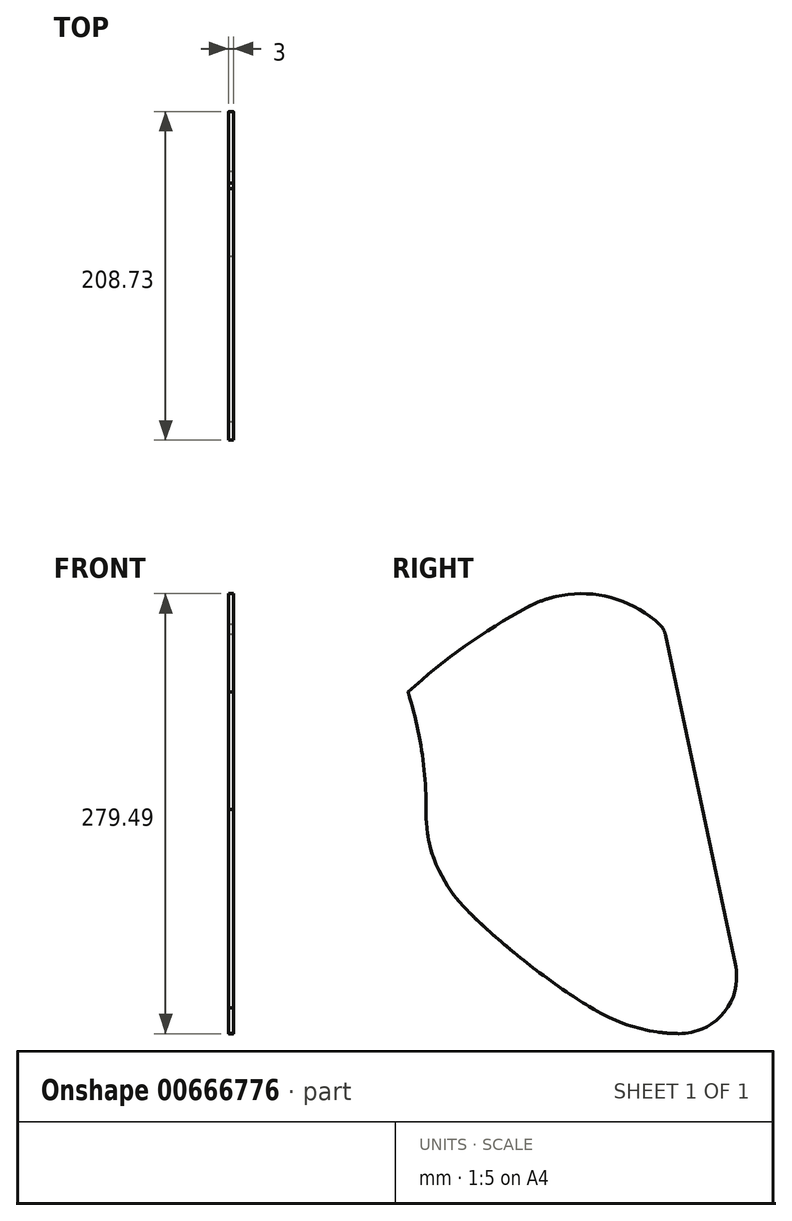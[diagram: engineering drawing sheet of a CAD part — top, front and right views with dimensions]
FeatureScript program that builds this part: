
annotation { "Feature Type Name" : "Feature", "Feature Type Description" : "" }
export const myFeature = defineFeature(function(context is Context, id is Id, definition is map)
    precondition{}
    {
        {
            var Q0;
            Q0=qCreatedBy(makeId("Right.planeOp"),FACE);
            var sketch = newSketch(context, id + "F0", { "sketchPlane" : qUnion([Q0])});
            skFitSpline(sketch, "E0.0.0", {"points": [v(85.03, -159.67) * mm, v(86.53, -159.72) * mm, v(88.77, -159.67) * mm, v(91.36, -159.4) * mm, v(92.84, -159.17) * mm, v(94.31, -158.9) * mm, v(96.13, -158.5) * mm, v(99.01, -157.69) * mm, v(102.5, -156.37) * mm, v(106.5, -154.32) * mm, v(111.5, -151.02) * mm, v(116.97, -145.87) * mm, v(122, -138.38) * mm, v(124.68, -131.36) * mm, v(125.84, -125.5) * mm, v(126.22, -121.02) * mm, v(126.1, -116.54) * mm, v(125.67, -113.58) * mm, v(125.37, -112.11) * mm]});
            skFitSpline(sketch, "E0.0.1", {"points": [v(125.43, -112.38) * mm, v(107.3, -27.05) * mm, v(89.16, 58.28) * mm, v(71.03, 143.61) * mm]});
            skFitSpline(sketch, "E0.0.2", {"points": [v(71.07, 143.42) * mm, v(70.97, 143.92) * mm, v(70.75, 144.66) * mm, v(70.35, 145.6) * mm, v(70, 146.28) * mm, v(69.6, 146.94) * mm, v(69, 147.76) * mm, v(68.48, 148.32) * mm, v(68.1, 148.67) * mm]});
            skFitSpline(sketch, "E0.0.3", {"points": [v(68.1, 148.67) * mm, v(66.5, 150.16) * mm, v(64.04, 152.28) * mm, v(60.59, 154.91) * mm, v(57.92, 156.79) * mm, v(55.18, 158.56) * mm, v(52.38, 160.22) * mm, v(49.52, 161.77) * mm, v(46.6, 163.2) * mm, v(43.61, 164.53) * mm, v(40.59, 165.74) * mm, v(37.52, 166.83) * mm, v(34.4, 167.8) * mm, v(31.26, 168.64) * mm, v(28.08, 169.36) * mm, v(24.89, 169.96) * mm, v(21.66, 170.44) * mm, v(18.42, 170.78) * mm, v(15.17, 171) * mm, v(11.92, 171.1) * mm, v(8.65, 171.07) * mm, v(5.4, 170.91) * mm, v(2.15, 170.63) * mm, v(-1.07, 170.22) * mm, v(-4.3, 169.68) * mm, v(-7.48, 169.02) * mm, v(-10.64, 168.23) * mm, v(-13.77, 167.33) * mm, v(-16.86, 166.3) * mm, v(-19.92, 165.15) * mm, v(-23.92, 163.47) * mm, v(-26.84, 162.03) * mm, v(-28.75, 161) * mm]});
            skFitSpline(sketch, "E0.0.8", {"points": [v(-104.3, 9.13) * mm, v(-104.32, 7.36) * mm, v(-104.26, 3.82) * mm, v(-103.9, -1.48) * mm, v(-103.27, -6.75) * mm, v(-102.38, -11.98) * mm, v(-101.22, -17.17) * mm, v(-99.8, -22.28) * mm, v(-98.13, -27.32) * mm, v(-96.2, -32.27) * mm, v(-94.04, -37.12) * mm, v(-91.62, -41.85) * mm, v(-88.98, -46.45) * mm, v(-86.1, -50.92) * mm, v(-83, -55.23) * mm, v(-79.69, -59.38) * mm, v(-76.17, -63.36) * mm, v(-73.7, -65.9) * mm, v(-72.43, -67.13) * mm]});
            skFitSpline(sketch, "E0.0.9", {"points": [v(-72.44, -67.12) * mm, v(-65.3, -74.06) * mm, v(-54.3, -84.18) * mm, v(-41.03, -95.45) * mm, v(-33.31, -101.74) * mm, v(-27.46, -106.39) * mm, v(-21.54, -110.95) * mm, v(-13.57, -116.92) * mm, v(0.58, -127.08) * mm, v(13.05, -135.3) * mm, v(21.51, -140.56) * mm]});
            skFitSpline(sketch, "E0.0.10", {"points": [v(21.51, -140.56) * mm, v(23.9, -142.03) * mm, v(27.53, -144.13) * mm, v(32.5, -146.67) * mm, v(36.3, -148.46) * mm, v(40.15, -150.13) * mm, v(44.05, -151.66) * mm, v(48, -153.06) * mm, v(52, -154.34) * mm, v(56.04, -155.48) * mm, v(60.1, -156.5) * mm, v(64.2, -157.36) * mm, v(68.34, -158.1) * mm, v(72.5, -158.7) * mm, v(78.05, -159.33) * mm, v(82.24, -159.59) * mm, v(85.04, -159.67) * mm]});
            skArc(sketch, "E1", {"start": v(-28.75, 161) * mm, "mid": v(-75, 132.3) * mm, "end": v(-117.51, 98.34) * mm});
            skArc(sketch, "E2", {"start": v(-104.3, 9.13) * mm, "mid": v(-107.6, 54.22) * mm, "end": v(-117.51, 98.34) * mm});
            skFitSpline(sketch, "E3.0", {"points": [v(71.5, 152.34) * mm, v(69.82, 153.9) * mm, v(67.2, 156.16) * mm, v(63.54, 158.95) * mm, v(60.72, 160.93) * mm, v(57.81, 162.81) * mm, v(54.85, 164.57) * mm, v(51.81, 166.21) * mm, v(48.71, 167.74) * mm, v(45.55, 169.14) * mm, v(42.35, 170.42) * mm, v(39.1, 171.57) * mm, v(35.8, 172.6) * mm, v(32.46, 173.5) * mm, v(29.1, 174.26) * mm, v(25.7, 174.9) * mm, v(22.29, 175.4) * mm, v(18.85, 175.77) * mm, v(15.41, 176) * mm, v(11.96, 176.1) * mm, v(8.5, 176.07) * mm, v(5.06, 175.9) * mm, v(1.62, 175.6) * mm, v(-1.8, 175.16) * mm, v(-5.21, 174.6) * mm, v(-8.6, 173.9) * mm, v(-11.94, 173.06) * mm, v(-15.25, 172.1) * mm, v(-18.53, 171.01) * mm, v(-21.77, 169.8) * mm, v(-26, 168.01) * mm, v(-29.1, 166.49) * mm, v(-31.13, 165.39) * mm]});
            skFitSpline(sketch, "E3.1", {"points": [v(75.96, 144.45) * mm, v(75.8, 145.2) * mm, v(75.38, 146.68) * mm, v(74.4, 148.77) * mm, v(73.1, 150.68) * mm, v(72.07, 151.81) * mm, v(71.5, 152.34) * mm]});
            skArc(sketch, "E3.2", {"start": v(-31.13, 165.39) * mm, "mid": v(-79.18, 135.46) * mm, "end": v(-123.23, 99.9) * mm});
            skFitSpline(sketch, "E3.3", {"points": [v(130.32, -111.34) * mm, v(112.19, -26.01) * mm, v(94.06, 59.32) * mm, v(75.92, 144.65) * mm]});
            skFitSpline(sketch, "E3.4", {"points": [v(84.86, -164.66) * mm, v(86.54, -164.72) * mm, v(89.06, -164.67) * mm, v(92.4, -164.3) * mm, v(94.9, -163.9) * mm, v(97.36, -163.35) * mm, v(100.6, -162.43) * mm, v(106.11, -160.36) * mm, v(113.42, -156.09) * mm, v(120.81, -149.13) * mm, v(126.47, -140.7) * mm, v(130.1, -131.22) * mm, v(131.28, -122.84) * mm, v(131.08, -116.11) * mm, v(130.6, -112.78) * mm, v(130.28, -111.13) * mm]});
            skArc(sketch, "E3.5", {"start": v(-109.3, 9.15) * mm, "mid": v(-112.78, 55.06) * mm, "end": v(-123.23, 99.9) * mm});
            skFitSpline(sketch, "E3.6", {"points": [v(-109.3, 9.17) * mm, v(-109.32, 7.32) * mm, v(-109.26, 3.6) * mm, v(-108.75, -3.8) * mm, v(-106.9, -16.65) * mm, v(-102.56, -30.9) * mm, v(-96.14, -44.3) * mm, v(-90.35, -53.81) * mm, v(-84.75, -61.21) * mm, v(-79.84, -66.77) * mm, v(-77.24, -69.42) * mm, v(-75.91, -70.71) * mm]});
            skFitSpline(sketch, "E3.7", {"points": [v(-75.92, -70.7) * mm, v(-68.71, -77.71) * mm, v(-57.63, -87.92) * mm, v(-42.32, -100.92) * mm, v(-30.57, -110.36) * mm, v(-18.56, -119.5) * mm, v(-2.25, -131.2) * mm, v(10.33, -139.5) * mm, v(18.88, -144.8) * mm]});
            skFitSpline(sketch, "E3.8", {"points": [v(18.88, -144.8) * mm, v(21.35, -146.34) * mm, v(25.12, -148.51) * mm, v(30.3, -151.16) * mm, v(34.24, -153.02) * mm, v(38.25, -154.75) * mm, v(42.3, -156.34) * mm, v(46.4, -157.8) * mm, v(50.56, -159.13) * mm, v(54.76, -160.32) * mm, v(58.99, -161.36) * mm, v(63.25, -162.27) * mm, v(67.54, -163.04) * mm, v(71.86, -163.67) * mm, v(77.63, -164.31) * mm, v(81.98, -164.58) * mm, v(84.9, -164.66) * mm]});
            skSolve(sketch);
        }
        {
            var Q0;
            Q0=qSketchRegion(id+"F0",true);
            extrude(context, id + "F1", {"entities" : qUnion([Q0]), "depth" : 192.68 * mm, "offsetDistance" : 25 * mm});
        }
        {
            var Q0;
            Q0=makeQuery(id+"F1.opExtrude","SWEPT_BODY",BODY,{"disambiguationData":[OSD([sQuery(id+"F0.wireOp",EDGE,"E0.0.0"),sQuery(id+"F0.wireOp",EDGE,"E0.0.1"),sQuery(id+"F0.wireOp",EDGE,"E0.0.2"),sQuery(id+"F0.wireOp",EDGE,"E0.0.3"),sQuery(id+"F0.wireOp",EDGE,"E0.0.8"),sQuery(id+"F0.wireOp",EDGE,"E0.0.9"),sQuery(id+"F0.wireOp",EDGE,"E0.0.10"),sQuery(id+"F0.wireOp",EDGE,"E1"),sQuery(id+"F0.wireOp",EDGE,"E2")])]});
            var Q1;
            Q1=qCreatedBy(makeId("Origin.pointOp"),VERTEX);
            var Q2;
            Q2=qCreatedBy(makeId("Origin.pointOp"),VERTEX);
            transform(context, id + "F2", {"entities" : qUnion([Q0]), "transformType" : TransformType.SCALE_UNIFORMLY, "scale" : 0.82, "scalePoint" : qUnion([Q2]), "makeCopy" : false});
        }
        {
            var Q0;
            Q0=makeQuery(id+"F1.opExtrude","SWEPT_FACE",FACE,{"disambiguationData":[OSD([sQuery(id+"F0.wireOp",EDGE,"E3.3")])]});
            var sketch = newSketch(context, id + "F3", { "sketchPlane" : qUnion([Q0])});
            skFitSpline(sketch, "E4.0", {"points": [v(-158, -111.52) * mm, v(-158, -39.99) * mm, v(-158, 31.55) * mm, v(-158, 103.08) * mm], "construction": true});
            skFitSpline(sketch, "E5.0", {"points": [v(0, -111.52) * mm, v(0, -39.99) * mm, v(0, 31.55) * mm, v(0, 103.08) * mm], "construction": true});
            skCircle(sketch, "E6", {"center": v(-79, -26.35) * mm, "radius": 32.5 * mm});
            skSolve(sketch);
        }
        {
            var Q0;
            Q0=makeQuery(id+"F1.opExtrude","SWEPT_FACE",FACE,{"disambiguationData":[OSD([sQuery(id+"F0.wireOp",EDGE,"E3.3")])]});
            var sketch = newSketch(context, id + "F4", { "sketchPlane" : qUnion([Q0])});
            skCircle(sketch, "E7", {"center": v(-82, -21.35) * mm, "radius": 30 * mm});
            skFitSpline(sketch, "E8.0", {"points": [v(-158, -111.52) * mm, v(-158, -39.99) * mm, v(-158, 31.55) * mm, v(-158, 103.08) * mm], "construction": true});
            skFitSpline(sketch, "E9.0", {"points": [v(0, -111.52) * mm, v(0, -39.99) * mm, v(0, 31.55) * mm, v(0, 103.08) * mm], "construction": true});
            skSolve(sketch);
        }
        {
            var Q0;
            Q0=qSketchRegion(id+"F3",true);
            extrude(context, id + "F5", {"entities" : qUnion([Q0]), "operationType" : NewBodyOperationType.REMOVE, "oppositeDirection" : true, "depth" : 25 * mm, "offsetDistance" : 25 * mm});
        }
        {
            var Q0;
            Q0=qCreatedBy(makeId("Right.planeOp"),FACE);
            cPlane(context, id + "F6", {"entities" : qUnion([Q0]), "cplaneType" : CPlaneType.OFFSET, "offset" : 3 * mm, "width" : 150 * mm, "height" : 150 * mm});
        }
        {
            var Q0;
            Q0=qCreatedBy(makeId("Right.planeOp"),FACE);
            var sketch = newSketch(context, id + "F7", { "sketchPlane" : qUnion([Q0])});
            skFitSpline(sketch, "E10.0.0", {"points": [v(-62.26, -57.98) * mm, v(-56.34, -63.72) * mm, v(-47.26, -72.1) * mm, v(-34.7, -82.75) * mm, v(-25.06, -90.5) * mm, v(-15.22, -97.98) * mm, v(-1.85, -107.6) * mm, v(8.47, -114.39) * mm, v(15.48, -118.74) * mm]});
            skFitSpline(sketch, "E10.0.1", {"points": [v(15.48, -118.74) * mm, v(17.5, -120) * mm, v(20.6, -121.78) * mm, v(24.84, -123.95) * mm, v(28.08, -125.48) * mm, v(31.36, -126.9) * mm, v(34.69, -128.2) * mm, v(38.05, -129.4) * mm, v(41.46, -130.49) * mm, v(44.9, -131.46) * mm, v(48.37, -132.32) * mm, v(51.86, -133.06) * mm, v(55.38, -133.7) * mm, v(58.92, -134.2) * mm, v(63.66, -134.74) * mm, v(67.23, -134.96) * mm, v(69.61, -135.02) * mm]});
            skFitSpline(sketch, "E10.0.2", {"points": [v(69.58, -135.02) * mm, v(70.96, -135.07) * mm, v(73.03, -135.03) * mm, v(75.77, -134.73) * mm, v(77.82, -134.4) * mm, v(79.83, -133.95) * mm, v(82.49, -133.2) * mm, v(87.01, -131.5) * mm, v(93, -128) * mm, v(99.07, -122.29) * mm, v(103.7, -115.38) * mm, v(106.68, -107.6) * mm, v(107.65, -100.73) * mm, v(107.49, -95.21) * mm, v(107.1, -92.48) * mm, v(106.83, -91.12) * mm]});
            skFitSpline(sketch, "E10.0.3", {"points": [v(106.86, -91.3) * mm, v(92, -21.33) * mm, v(77.13, 48.64) * mm, v(62.26, 118.61) * mm], "construction": true});
            skFitSpline(sketch, "E10.0.4", {"points": [v(62.3, 118.45) * mm, v(62.16, 119.06) * mm, v(61.8, 120.27) * mm, v(61, 121.99) * mm, v(59.95, 123.56) * mm, v(59.1, 124.49) * mm, v(58.63, 124.92) * mm]});
            skFitSpline(sketch, "E10.0.5", {"points": [v(58.63, 124.92) * mm, v(57.25, 126.2) * mm, v(55.1, 128.05) * mm, v(52.1, 130.34) * mm, v(49.79, 131.97) * mm, v(47.4, 133.5) * mm, v(44.97, 134.95) * mm, v(42.49, 136.3) * mm, v(39.94, 137.54) * mm, v(37.36, 138.7) * mm, v(34.73, 139.74) * mm, v(32.06, 140.69) * mm, v(29.36, 141.53) * mm, v(26.62, 142.27) * mm, v(23.86, 142.9) * mm, v(21.08, 143.41) * mm, v(18.28, 143.83) * mm, v(15.46, 144.13) * mm, v(12.64, 144.32) * mm, v(9.81, 144.4) * mm, v(6.98, 144.38) * mm, v(4.15, 144.24) * mm, v(1.33, 144) * mm, v(-1.48, 143.64) * mm, v(-4.27, 143.17) * mm, v(-7.05, 142.6) * mm, v(-9.8, 141.91) * mm, v(-12.5, 141.13) * mm, v(-15.2, 140.23) * mm, v(-17.85, 139.23) * mm, v(-21.33, 137.77) * mm, v(-23.87, 136.52) * mm, v(-25.53, 135.62) * mm]});
            skArc(sketch, "E10.0.6", {"start": v(-25.53, 135.62) * mm, "mid": v(-64.93, 111.07) * mm, "end": v(-101.05, 81.92) * mm, "construction": true});
            skArc(sketch, "E10.0.7", {"start": v(-101.05, 81.92) * mm, "mid": v(-92.48, 45.15) * mm, "end": v(-89.63, 7.5) * mm, "construction": true});
            skFitSpline(sketch, "E10.0.8", {"points": [v(-89.63, 7.52) * mm, v(-89.64, 6) * mm, v(-89.6, 2.96) * mm, v(-89.18, -3.1) * mm, v(-87.65, -13.65) * mm, v(-84.1, -25.35) * mm, v(-78.84, -36.33) * mm, v(-74.09, -44.13) * mm, v(-69.5, -50.2) * mm, v(-65.46, -54.75) * mm, v(-63.34, -56.92) * mm, v(-62.25, -57.98) * mm], "construction": true});
            skArc(sketch, "E11.0", {"start": v(-96.36, 80.64) * mm, "mid": v(-88.17, 44.08) * mm, "end": v(-85.54, 6.7) * mm});
            skArc(sketch, "E11.1", {"start": v(-23.58, 132.01) * mm, "mid": v(-61.5, 108.48) * mm, "end": v(-96.36, 80.64) * mm});
            skFitSpline(sketch, "E11.2", {"points": [v(-85.53, 7.49) * mm, v(-85.54, 6.04) * mm, v(-85.5, 3.14) * mm, v(-85.1, -2.66) * mm, v(-83.64, -12.72) * mm, v(-80.25, -23.89) * mm, v(-75.23, -34.37) * mm, v(-70.7, -41.81) * mm, v(-66.3, -47.6) * mm, v(-62.46, -51.96) * mm, v(-60.43, -54.03) * mm, v(-59.4, -55.04) * mm]});
            skFitSpline(sketch, "E11.3", {"points": [v(55.84, 121.91) * mm, v(54.53, 123.13) * mm, v(52.5, 124.87) * mm, v(49.68, 127.03) * mm, v(47.5, 128.57) * mm, v(45.25, 130.02) * mm, v(42.95, 131.38) * mm, v(40.6, 132.65) * mm, v(38.2, 133.83) * mm, v(35.76, 134.92) * mm, v(33.28, 135.9) * mm, v(30.77, 136.8) * mm, v(28.21, 137.6) * mm, v(25.63, 138.29) * mm, v(23.03, 138.88) * mm, v(20.4, 139.37) * mm, v(17.76, 139.76) * mm, v(15.1, 140.04) * mm, v(12.44, 140.23) * mm, v(9.77, 140.3) * mm, v(7.1, 140.28) * mm, v(4.43, 140.15) * mm, v(1.77, 139.91) * mm, v(-0.88, 139.58) * mm, v(-3.52, 139.14) * mm, v(-6.14, 138.6) * mm, v(-8.73, 137.95) * mm, v(-11.3, 137.2) * mm, v(-13.83, 136.37) * mm, v(-16.33, 135.42) * mm, v(-19.61, 134.04) * mm, v(-22, 132.86) * mm, v(-23.58, 132.01) * mm]});
            skFitSpline(sketch, "E11.4", {"points": [v(58.28, 117.6) * mm, v(58.2, 118.01) * mm, v(58.02, 118.62) * mm, v(57.7, 119.39) * mm, v(57.4, 119.95) * mm, v(57.07, 120.49) * mm, v(56.58, 121.16) * mm, v(56.15, 121.63) * mm, v(55.84, 121.91) * mm]});
            skFitSpline(sketch, "E11.5", {"points": [v(-59.4, -55.04) * mm, v(-53.54, -60.73) * mm, v(-44.53, -69.03) * mm, v(-32.1, -79.6) * mm, v(-22.54, -87.27) * mm, v(-12.78, -94.68) * mm, v(0.47, -104.2) * mm, v(10.7, -110.95) * mm, v(17.64, -115.26) * mm]});
            skFitSpline(sketch, "E11.6", {"points": [v(17.64, -115.26) * mm, v(19.6, -116.47) * mm, v(22.57, -118.18) * mm, v(26.65, -120.27) * mm, v(29.76, -121.74) * mm, v(32.92, -123.1) * mm, v(36.12, -124.36) * mm, v(39.36, -125.51) * mm, v(42.64, -126.56) * mm, v(45.95, -127.5) * mm, v(49.29, -128.32) * mm, v(52.65, -129.04) * mm, v(56.04, -129.64) * mm, v(59.45, -130.14) * mm, v(64, -130.65) * mm, v(67.43, -130.86) * mm, v(69.73, -130.93) * mm]});
            skFitSpline(sketch, "E11.7", {"points": [v(69.72, -130.93) * mm, v(70.95, -130.97) * mm, v(72.79, -130.93) * mm, v(75.22, -130.67) * mm, v(77.04, -130.37) * mm, v(78.83, -129.97) * mm, v(81.19, -129.3) * mm, v(85.2, -127.8) * mm, v(90.53, -124.68) * mm, v(95.91, -119.61) * mm, v(100.03, -113.47) * mm, v(102.68, -106.57) * mm, v(103.54, -100.46) * mm, v(103.4, -95.56) * mm, v(103.05, -93.13) * mm, v(102.8, -91.93) * mm]});
            skFitSpline(sketch, "E11.8", {"points": [v(102.85, -92.15) * mm, v(87.98, -22.18) * mm, v(73.12, 47.79) * mm, v(58.25, 117.76) * mm]});
            skSolve(sketch);
        }
        {
            var Q0;
            Q0=qCreatedBy(id+"F6.planeOp",FACE);
            var sketch = newSketch(context, id + "F8", { "sketchPlane" : qUnion([Q0])});
            skLineSegment(sketch, "E12", {"start": v(-96.16, 80.21) * mm, "end": v(-25.08, -79.7) * mm});
            skLineSegment(sketch, "E13", {"start": v(-25.08, -79.7) * mm, "end": v(-58.13, -94.4) * mm});
            skLineSegment(sketch, "E14", {"start": v(-58.13, -94.4) * mm, "end": v(-129.2, 65.52) * mm});
            skLineSegment(sketch, "E15", {"start": v(-129.2, 65.52) * mm, "end": v(-96.16, 80.21) * mm});
            skSolve(sketch);
        }
        {
            var Q0;
            Q0=qSketchRegion(id+"F8",true);
            extrude(context, id + "F9", {"entities" : qUnion([Q0]), "operationType" : NewBodyOperationType.REMOVE, "depth" : 158 * mm, "offsetDistance" : 25 * mm, "hasSecondDirection" : true, "secondDirectionOppositeDirection" : true, "secondDirectionDepth" : 25 * mm});
        }
        {
            var Q0;
            Q0=makeQuery(id+"F1.opExtrude","CAP_FACE",FACE,{"disambiguationData":[OSD([sQuery(id+"F0.wireOp",EDGE,"E0.0.0"),sQuery(id+"F0.wireOp",EDGE,"E0.0.1"),sQuery(id+"F0.wireOp",EDGE,"E0.0.2"),sQuery(id+"F0.wireOp",EDGE,"E0.0.3"),sQuery(id+"F0.wireOp",EDGE,"E0.0.8"),sQuery(id+"F0.wireOp",EDGE,"E0.0.9"),sQuery(id+"F0.wireOp",EDGE,"E0.0.10"),sQuery(id+"F0.wireOp",EDGE,"E1"),sQuery(id+"F0.wireOp",EDGE,"E2"),sQuery(id+"F0.wireOp",EDGE,"E3.0"),sQuery(id+"F0.wireOp",EDGE,"E3.1"),sQuery(id+"F0.wireOp",EDGE,"E3.2"),sQuery(id+"F0.wireOp",EDGE,"E3.3"),sQuery(id+"F0.wireOp",EDGE,"E3.4"),sQuery(id+"F0.wireOp",EDGE,"E3.5"),sQuery(id+"F0.wireOp",EDGE,"E3.6"),sQuery(id+"F0.wireOp",EDGE,"E3.7"),sQuery(id+"F0.wireOp",EDGE,"E3.8")])],"isStart":false});
            var sketch = newSketch(context, id + "F10", { "sketchPlane" : qUnion([Q0])});
            skLineSegment(sketch, "E16", {"start": v(-96.22, 80.18) * mm, "end": v(-29.48, -81.66) * mm, "construction": true});
            skLineSegment(sketch, "E17.0", {"start": v(-89.75, 82.85) * mm, "end": v(-23.01, -79) * mm, "construction": true});
            skLineSegment(sketch, "E18", {"start": v(-96.22, 80.18) * mm, "end": v(-96.89, 81.67) * mm});
            skLineSegment(sketch, "E19", {"start": v(-96.89, 81.67) * mm, "end": v(-91.34, 86.7) * mm});
            skLineSegment(sketch, "E20", {"start": v(-89.75, 82.85) * mm, "end": v(-91.34, 86.7) * mm});
            skLineSegment(sketch, "E21", {"start": v(-89.75, 82.85) * mm, "end": v(-17.3, -92.82) * mm});
            skLineSegment(sketch, "E22", {"start": v(-17.3, -92.82) * mm, "end": v(-29.48, -83.53) * mm});
            skLineSegment(sketch, "E23", {"start": v(-29.48, -83.53) * mm, "end": v(-29.48, -81.66) * mm});
            skLineSegment(sketch, "E24", {"start": v(-29.48, -81.66) * mm, "end": v(-96.22, 80.18) * mm});
            skLineSegment(sketch, "E25", {"start": v(-94.61, 76.28) * mm, "end": v(-88.21, 79.12) * mm});
            skLineSegment(sketch, "E26", {"start": v(-30.73, -78.64) * mm, "end": v(-24.26, -75.97) * mm});
            skSolve(sketch);
        }
        {
            var Q0;
            {var subQ0=sQuery(id+"F10.wireOp",EDGE,"E25");Q0=makeQuery(id+"F10.imprint","IMPRINT",FACE,{"disambiguationData":[TD([[makeQuery(id+"F10.imprint","IMPRINT",EDGE,{"derivedFrom":subQ0}),1.0]])]});}
            var Q1;
            {var subQ0=sQuery(id+"F10.wireOp",EDGE,"E26");Q1=makeQuery(id+"F10.imprint","IMPRINT",FACE,{"disambiguationData":[TD([[makeQuery(id+"F10.imprint","IMPRINT",EDGE,{"derivedFrom":subQ0}),-1.0]])]});}
            extrude(context, id + "F11", {"entities" : qUnion([Q0, Q1]), "operationType" : NewBodyOperationType.ADD, "oppositeDirection" : true, "depth" : 158 * mm, "offsetDistance" : 25 * mm});
        }
        {
            var Q0;
            {var subQ0=sQuery(id+"F10.wireOp",EDGE,"E24");var subQ1=sQuery(id+"F10.wireOp",EDGE,"E21");var subQ2=sQuery(id+"F0.wireOp",EDGE,"E0.0.9");var subQ3=sQuery(id+"F0.wireOp",EDGE,"E2");var subQ4=sQuery(id+"F0.wireOp",EDGE,"E1");Q0=makeQuery(id+"F11.boolean.opBoolean","MERGE",FACE,{"derivedFrom":[makeQuery(id+"F1.opExtrude","CAP_FACE",FACE,{"disambiguationData":[OSD([sQuery(id+"F0.wireOp",EDGE,"E0.0.0"),sQuery(id+"F0.wireOp",EDGE,"E0.0.1"),sQuery(id+"F0.wireOp",EDGE,"E0.0.2"),sQuery(id+"F0.wireOp",EDGE,"E0.0.3"),sQuery(id+"F0.wireOp",EDGE,"E0.0.8"),subQ2,sQuery(id+"F0.wireOp",EDGE,"E0.0.10"),subQ4,subQ3,sQuery(id+"F0.wireOp",EDGE,"E3.0"),sQuery(id+"F0.wireOp",EDGE,"E3.1"),sQuery(id+"F0.wireOp",EDGE,"E3.2"),sQuery(id+"F0.wireOp",EDGE,"E3.3"),sQuery(id+"F0.wireOp",EDGE,"E3.4"),sQuery(id+"F0.wireOp",EDGE,"E3.5"),sQuery(id+"F0.wireOp",EDGE,"E3.6"),sQuery(id+"F0.wireOp",EDGE,"E3.7"),sQuery(id+"F0.wireOp",EDGE,"E3.8")])],"isStart":false}),makeQuery(id+"F11.opExtrude","CAP_FACE",FACE,{"disambiguationData":[OSD([subQ4,subQ3,sQuery(id+"F10.wireOp",EDGE,"E20"),subQ1,subQ0,sQuery(id+"F10.wireOp",EDGE,"E25")])],"isStart":true}),makeQuery(id+"F11.opExtrude","CAP_FACE",FACE,{"disambiguationData":[OSD([subQ2,subQ1,subQ0,sQuery(id+"F10.wireOp",EDGE,"E26")])],"isStart":true})]});}
            var sketch = newSketch(context, id + "F12", { "sketchPlane" : qUnion([Q0])});
            skLineSegment(sketch, "E27", {"start": v(-29.48, -81.66) * mm, "end": v(-96.22, 80.18) * mm});
            skLineSegment(sketch, "E28", {"start": v(-96.22, 80.18) * mm, "end": v(-100, 78.5) * mm});
            skLineSegment(sketch, "E29", {"start": v(-100, 78.5) * mm, "end": v(-29.48, -92.5) * mm});
            skSolve(sketch);
        }
        {
            var Q0;
            Q0=qCreatedBy(makeId("Right.planeOp"),FACE);
            var sketch = newSketch(context, id + "F13", { "sketchPlane" : qUnion([Q0])});
            skArc(sketch, "E30.0", {"start": v(-25.53, 135.62) * mm, "mid": v(-64.93, 111.07) * mm, "end": v(-101.05, 81.92) * mm});
            skPoint(sketch, "E31.0", {"position": v(-92.48, 45.15) * mm});
            skArc(sketch, "E32.0", {"start": v(-101.05, 81.92) * mm, "mid": v(-92.48, 45.15) * mm, "end": v(-89.63, 7.5) * mm});
            skFitSpline(sketch, "E33.0", {"points": [v(-89.63, 7.52) * mm, v(-89.64, 6) * mm, v(-89.6, 2.96) * mm, v(-89.18, -3.1) * mm, v(-87.65, -13.65) * mm, v(-84.1, -25.35) * mm, v(-78.84, -36.33) * mm, v(-74.09, -44.13) * mm, v(-69.5, -50.2) * mm, v(-65.46, -54.75) * mm, v(-63.34, -56.92) * mm, v(-62.25, -57.98) * mm]});
            skFitSpline(sketch, "E34.0", {"points": [v(-62.26, -57.98) * mm, v(-56.34, -63.72) * mm, v(-47.26, -72.1) * mm, v(-34.7, -82.75) * mm, v(-25.06, -90.5) * mm, v(-15.22, -97.98) * mm, v(-1.85, -107.6) * mm, v(8.47, -114.39) * mm, v(15.48, -118.74) * mm]});
            skFitSpline(sketch, "E35.0", {"points": [v(-62.26, -57.98) * mm, v(-56.34, -63.72) * mm, v(-47.26, -72.1) * mm, v(-34.7, -82.75) * mm, v(-25.06, -90.5) * mm, v(-15.22, -97.98) * mm, v(-1.85, -107.6) * mm, v(8.47, -114.39) * mm, v(15.48, -118.74) * mm]});
            skFitSpline(sketch, "E36.0", {"points": [v(15.48, -118.74) * mm, v(17.5, -120) * mm, v(20.6, -121.78) * mm, v(24.84, -123.95) * mm, v(28.08, -125.48) * mm, v(31.36, -126.9) * mm, v(34.69, -128.2) * mm, v(38.05, -129.4) * mm, v(41.46, -130.49) * mm, v(44.9, -131.46) * mm, v(48.37, -132.32) * mm, v(51.86, -133.06) * mm, v(55.38, -133.7) * mm, v(58.92, -134.2) * mm, v(63.66, -134.74) * mm, v(67.23, -134.96) * mm, v(69.61, -135.02) * mm]});
            skFitSpline(sketch, "E37.0", {"points": [v(69.58, -135.02) * mm, v(70.96, -135.07) * mm, v(73.03, -135.03) * mm, v(75.77, -134.73) * mm, v(77.82, -134.4) * mm, v(79.83, -133.95) * mm, v(82.49, -133.2) * mm, v(87.01, -131.5) * mm, v(93, -128) * mm, v(99.07, -122.29) * mm, v(103.7, -115.38) * mm, v(106.68, -107.6) * mm, v(107.65, -100.73) * mm, v(107.49, -95.21) * mm, v(107.1, -92.48) * mm, v(106.83, -91.12) * mm]});
            skFitSpline(sketch, "E38.0", {"points": [v(106.86, -91.3) * mm, v(92, -21.33) * mm, v(77.13, 48.64) * mm, v(62.26, 118.61) * mm]});
            skFitSpline(sketch, "E39.0", {"points": [v(62.3, 118.45) * mm, v(62.16, 119.06) * mm, v(61.8, 120.27) * mm, v(61, 121.99) * mm, v(59.95, 123.56) * mm, v(59.1, 124.49) * mm, v(58.63, 124.92) * mm]});
            skFitSpline(sketch, "E40.0", {"points": [v(58.63, 124.92) * mm, v(57.25, 126.2) * mm, v(55.1, 128.05) * mm, v(52.1, 130.34) * mm, v(49.79, 131.97) * mm, v(47.4, 133.5) * mm, v(44.97, 134.95) * mm, v(42.49, 136.3) * mm, v(39.94, 137.54) * mm, v(37.36, 138.7) * mm, v(34.73, 139.74) * mm, v(32.06, 140.69) * mm, v(29.36, 141.53) * mm, v(26.62, 142.27) * mm, v(23.86, 142.9) * mm, v(21.08, 143.41) * mm, v(18.28, 143.83) * mm, v(15.46, 144.13) * mm, v(12.64, 144.32) * mm, v(9.81, 144.4) * mm, v(6.98, 144.38) * mm, v(4.15, 144.24) * mm, v(1.33, 144) * mm, v(-1.48, 143.64) * mm, v(-4.27, 143.17) * mm, v(-7.05, 142.6) * mm, v(-9.8, 141.91) * mm, v(-12.5, 141.13) * mm, v(-15.2, 140.23) * mm, v(-17.85, 139.23) * mm, v(-21.33, 137.77) * mm, v(-23.87, 136.52) * mm, v(-25.53, 135.62) * mm]});
            skSolve(sketch);
        }
        {
            var Q0;
            Q0 = qSketchRegion(id + "F13", true);
            extrude(context, id + "F14", {"entities" : qUnion([Q0]), "operationType" : NewBodyOperationType.ADD, "depth" : 3 * mm, "offsetDistance" : 25 * mm});
        }
        {
            var Q0;
            Q0=makeQuery(id+"F12.imprint","IMPRINT",FACE,{"disambiguationData":[TD([[makeQuery(id+"F12.imprint","IMPRINT",EDGE,{"derivedFrom":makeQuery(id+"F1.opExtrude","CAP_EDGE",EDGE,{"disambiguationData":[OSD([sQuery(id+"F0.wireOp",EDGE,"E0.0.0")])],"isStart":false})}),1.0]])]});
            var sketch = newSketch(context, id + "F15", { "sketchPlane" : qUnion([Q0])});
            skLineSegment(sketch, "E41.bottom", {"start": v(-129.8, 180.6) * mm, "end": v(129.8, 180.6) * mm});
            skLineSegment(sketch, "E41.top", {"start": v(-129.8, -180.6) * mm, "end": v(129.8, -180.6) * mm});
            skLineSegment(sketch, "E41.left", {"start": v(-129.8, 180.6) * mm, "end": v(-129.8, -180.6) * mm});
            skLineSegment(sketch, "E41.right", {"start": v(129.8, 180.6) * mm, "end": v(129.8, -180.6) * mm});
            skPoint(sketch, "E41.middle", {"position": v(0, 0) * mm});
            skSolve(sketch);
        }
        {
            var Q0;
            Q0 = qSketchRegion(id + "F15", true);
            extrude(context, id + "F16", {"entities" : qUnion([Q0]), "operationType" : NewBodyOperationType.REMOVE, "oppositeDirection" : true, "depth" : 155 * mm, "offsetDistance" : 25 * mm});
        }
    });
